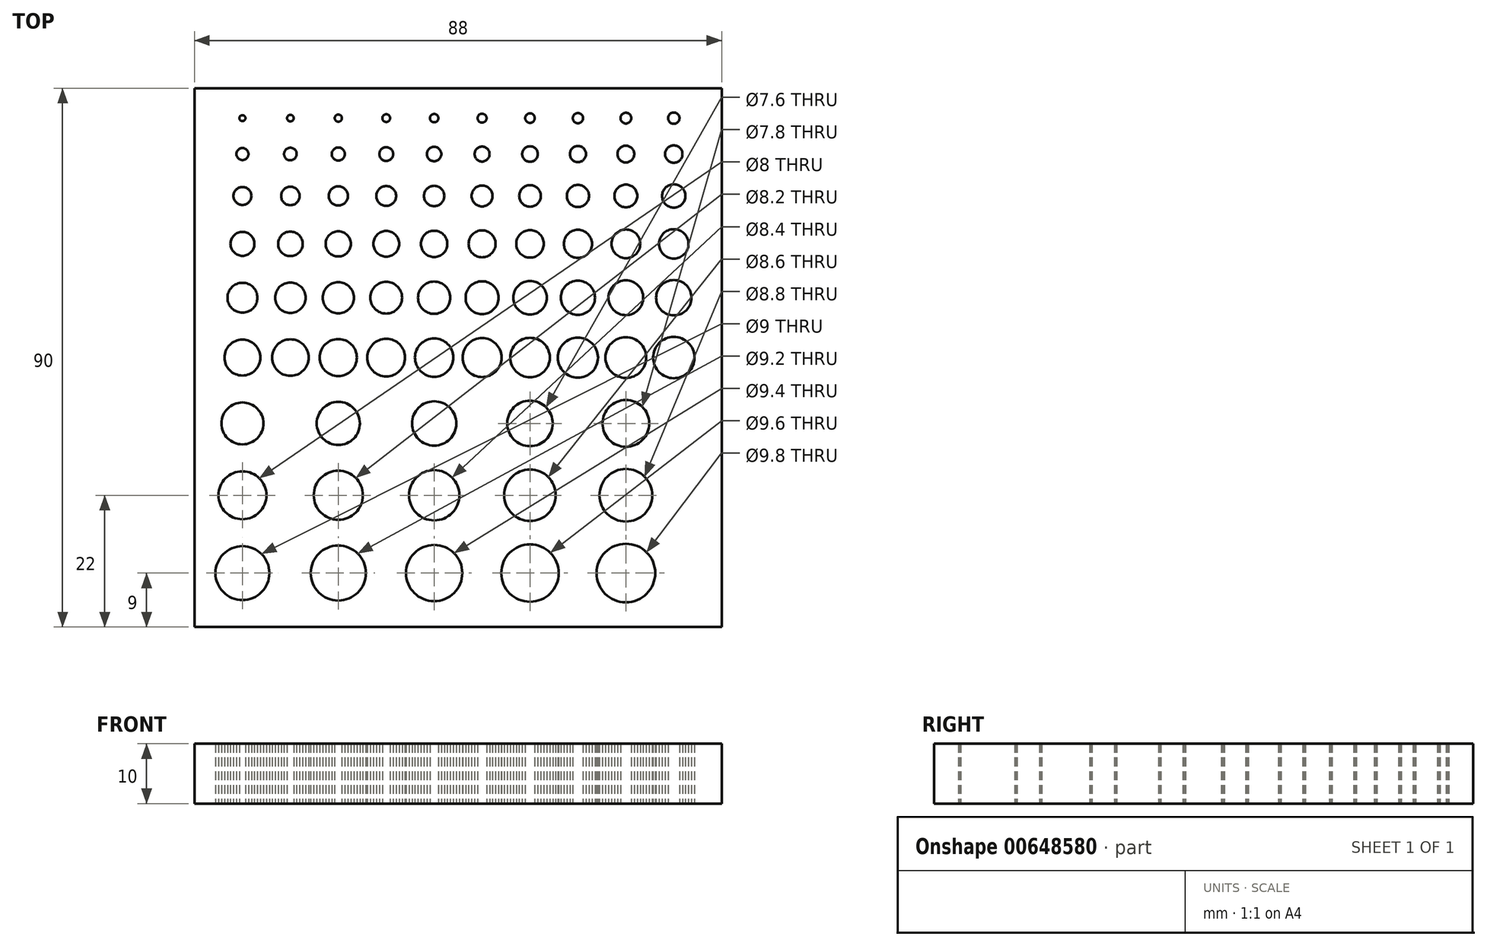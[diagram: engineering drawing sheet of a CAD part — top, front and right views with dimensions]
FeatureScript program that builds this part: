
annotation { "Feature Type Name" : "Feature", "Feature Type Description" : "" }
export const myFeature = defineFeature(function(context is Context, id is Id, definition is map)
    precondition{}
    {
        {
            var Q0;
            Q0=qCreatedBy(makeId("Top.planeOp"),FACE);
            var sketch = newSketch(context, id + "F0", { "sketchPlane" : qUnion([Q0])});
            skLineSegment(sketch, "E0.bottom", {"start": v(44, -45) * mm, "end": v(-44, -45) * mm});
            skLineSegment(sketch, "E0.top", {"start": v(44, 45) * mm, "end": v(-44, 45) * mm});
            skLineSegment(sketch, "E0.left", {"start": v(44, -45) * mm, "end": v(44, 45) * mm});
            skLineSegment(sketch, "E0.right", {"start": v(-44, -45) * mm, "end": v(-44, 45) * mm});
            skPoint(sketch, "E0.middle", {"position": v(0, 0) * mm});
            skLineSegment(sketch, "E1", {"start": v(-44, 40) * mm, "end": v(44, 40) * mm, "construction": true});
            skLineSegment(sketch, "E2", {"start": v(-44, 34) * mm, "end": v(44, 34) * mm, "construction": true});
            skLineSegment(sketch, "E3", {"start": v(-44, 27) * mm, "end": v(44, 27) * mm, "construction": true});
            skLineSegment(sketch, "E4", {"start": v(-44, 19) * mm, "end": v(44, 19) * mm, "construction": true});
            skLineSegment(sketch, "E5", {"start": v(-44, 10) * mm, "end": v(44, 10) * mm, "construction": true});
            skLineSegment(sketch, "E6", {"start": v(-44, 0) * mm, "end": v(44, 0) * mm, "construction": true});
            skLineSegment(sketch, "E7", {"start": v(-44, -11) * mm, "end": v(44, -11) * mm, "construction": true});
            skLineSegment(sketch, "E8", {"start": v(-44, -23) * mm, "end": v(44, -23) * mm, "construction": true});
            skLineSegment(sketch, "E9", {"start": v(-44, -36) * mm, "end": v(44, -36) * mm, "construction": true});
            skLineSegment(sketch, "E10", {"start": v(-44, -46) * mm, "end": v(44, -46) * mm, "construction": true});
            skLineSegment(sketch, "E11", {"start": v(-36, 45) * mm, "end": v(-36, -45) * mm, "construction": true});
            skLineSegment(sketch, "E12", {"start": v(-28, 45) * mm, "end": v(-28, -45) * mm, "construction": true});
            skLineSegment(sketch, "E13", {"start": v(-20, 45) * mm, "end": v(-20, -45) * mm, "construction": true});
            skLineSegment(sketch, "E14", {"start": v(-12, 45) * mm, "end": v(-12, -45) * mm, "construction": true});
            skLineSegment(sketch, "E15", {"start": v(36, 45) * mm, "end": v(36, -45) * mm, "construction": true});
            skLineSegment(sketch, "E16", {"start": v(-4, -45) * mm, "end": v(-4, 45) * mm, "construction": true});
            skLineSegment(sketch, "E17", {"start": v(4, 45) * mm, "end": v(4, -45) * mm, "construction": true});
            skLineSegment(sketch, "E18", {"start": v(12, 45) * mm, "end": v(12, -45) * mm, "construction": true});
            skLineSegment(sketch, "E19", {"start": v(20, 45) * mm, "end": v(20, -45) * mm, "construction": true});
            skLineSegment(sketch, "E20", {"start": v(28, 45) * mm, "end": v(28, -45) * mm, "construction": true});
            skCircle(sketch, "E21", {"center": v(-36, 40) * mm, "radius": 0.5 * mm});
            skCircle(sketch, "E22", {"center": v(-28, 40) * mm, "radius": 0.55 * mm});
            skCircle(sketch, "E23", {"center": v(-20, 40) * mm, "radius": 0.6 * mm});
            skCircle(sketch, "E24", {"center": v(-12, 40) * mm, "radius": 0.65 * mm});
            skCircle(sketch, "E25", {"center": v(-4, 40) * mm, "radius": 0.7 * mm});
            skCircle(sketch, "E26", {"center": v(4, 40) * mm, "radius": 0.75 * mm});
            skCircle(sketch, "E27", {"center": v(12, 40) * mm, "radius": 0.8 * mm});
            skCircle(sketch, "E28", {"center": v(20, 40) * mm, "radius": 0.85 * mm});
            skCircle(sketch, "E29", {"center": v(28, 40) * mm, "radius": 0.9 * mm});
            skCircle(sketch, "E30", {"center": v(36, 40) * mm, "radius": 0.95 * mm});
            skCircle(sketch, "E31", {"center": v(-36, 34) * mm, "radius": 1 * mm});
            skCircle(sketch, "E32", {"center": v(-28, 34) * mm, "radius": 1.05 * mm});
            skCircle(sketch, "E33", {"center": v(-20, 34) * mm, "radius": 1.1 * mm});
            skCircle(sketch, "E34", {"center": v(-12, 34) * mm, "radius": 1.15 * mm});
            skCircle(sketch, "E35", {"center": v(-4, 34) * mm, "radius": 1.2 * mm});
            skCircle(sketch, "E36", {"center": v(4, 34) * mm, "radius": 1.25 * mm});
            skCircle(sketch, "E37", {"center": v(12, 34) * mm, "radius": 1.3 * mm});
            skCircle(sketch, "E38", {"center": v(20, 34) * mm, "radius": 1.35 * mm});
            skCircle(sketch, "E39", {"center": v(28, 34) * mm, "radius": 1.4 * mm});
            skCircle(sketch, "E40", {"center": v(36, 34) * mm, "radius": 1.45 * mm});
            skCircle(sketch, "E41", {"center": v(-36, 27) * mm, "radius": 1.5 * mm});
            skCircle(sketch, "E42", {"center": v(-28, 27) * mm, "radius": 1.55 * mm});
            skCircle(sketch, "E43", {"center": v(-20, 27) * mm, "radius": 1.6 * mm});
            skCircle(sketch, "E44", {"center": v(-12, 27) * mm, "radius": 1.65 * mm});
            skCircle(sketch, "E45", {"center": v(-4, 27) * mm, "radius": 1.7 * mm});
            skCircle(sketch, "E46", {"center": v(4, 27) * mm, "radius": 1.75 * mm});
            skCircle(sketch, "E47", {"center": v(12, 27) * mm, "radius": 1.8 * mm});
            skCircle(sketch, "E48", {"center": v(20, 27) * mm, "radius": 1.85 * mm});
            skCircle(sketch, "E49", {"center": v(28, 27) * mm, "radius": 1.9 * mm});
            skCircle(sketch, "E50", {"center": v(36, 27) * mm, "radius": 1.95 * mm});
            skCircle(sketch, "E51", {"center": v(-36, 19) * mm, "radius": 2 * mm});
            skCircle(sketch, "E52", {"center": v(-28, 19) * mm, "radius": 2.05 * mm});
            skCircle(sketch, "E53", {"center": v(-20, 19) * mm, "radius": 2.1 * mm});
            skCircle(sketch, "E54", {"center": v(-12, 19) * mm, "radius": 2.15 * mm});
            skCircle(sketch, "E55", {"center": v(-4, 19) * mm, "radius": 2.2 * mm});
            skCircle(sketch, "E56", {"center": v(4, 19) * mm, "radius": 2.25 * mm});
            skCircle(sketch, "E57", {"center": v(12, 19) * mm, "radius": 2.3 * mm});
            skCircle(sketch, "E58", {"center": v(20, 19) * mm, "radius": 2.35 * mm});
            skCircle(sketch, "E59", {"center": v(28, 19) * mm, "radius": 2.4 * mm});
            skCircle(sketch, "E60", {"center": v(36, 19) * mm, "radius": 2.45 * mm});
            skCircle(sketch, "E61", {"center": v(-36, 10) * mm, "radius": 2.5 * mm});
            skCircle(sketch, "E62", {"center": v(-28, 10) * mm, "radius": 2.55 * mm});
            skCircle(sketch, "E63", {"center": v(-20, 10) * mm, "radius": 2.6 * mm});
            skCircle(sketch, "E64", {"center": v(-12, 10) * mm, "radius": 2.65 * mm});
            skCircle(sketch, "E65", {"center": v(-4, 10) * mm, "radius": 2.7 * mm});
            skCircle(sketch, "E66", {"center": v(4, 10) * mm, "radius": 2.75 * mm});
            skCircle(sketch, "E67", {"center": v(12, 10) * mm, "radius": 2.8 * mm});
            skCircle(sketch, "E68", {"center": v(20, 10) * mm, "radius": 2.85 * mm});
            skCircle(sketch, "E69", {"center": v(28, 10) * mm, "radius": 2.9 * mm});
            skCircle(sketch, "E70", {"center": v(36, 10) * mm, "radius": 2.95 * mm});
            skCircle(sketch, "E71", {"center": v(-36, 0) * mm, "radius": 3 * mm});
            skCircle(sketch, "E72", {"center": v(-28, 0) * mm, "radius": 3.05 * mm});
            skCircle(sketch, "E73", {"center": v(-20, 0) * mm, "radius": 3.1 * mm});
            skCircle(sketch, "E74", {"center": v(-12, 0) * mm, "radius": 3.15 * mm});
            skCircle(sketch, "E75", {"center": v(-4, 0) * mm, "radius": 3.2 * mm});
            skCircle(sketch, "E76", {"center": v(4, 0) * mm, "radius": 3.25 * mm});
            skCircle(sketch, "E77", {"center": v(12, 0) * mm, "radius": 3.3 * mm});
            skCircle(sketch, "E78", {"center": v(20, 0) * mm, "radius": 3.35 * mm});
            skCircle(sketch, "E79", {"center": v(28, 0) * mm, "radius": 3.4 * mm});
            skCircle(sketch, "E80", {"center": v(36, 0) * mm, "radius": 3.45 * mm});
            skCircle(sketch, "E81", {"center": v(-36, -11) * mm, "radius": 3.5 * mm});
            skCircle(sketch, "E82", {"center": v(-20, -11) * mm, "radius": 3.6 * mm});
            skCircle(sketch, "E83", {"center": v(-4, -11) * mm, "radius": 3.7 * mm});
            skCircle(sketch, "E84", {"center": v(12, -11) * mm, "radius": 3.8 * mm});
            skCircle(sketch, "E85", {"center": v(28, -11) * mm, "radius": 3.9 * mm});
            skCircle(sketch, "E86", {"center": v(-36, -23) * mm, "radius": 4 * mm});
            skCircle(sketch, "E87", {"center": v(-20, -23) * mm, "radius": 4.1 * mm});
            skCircle(sketch, "E88", {"center": v(-4, -23) * mm, "radius": 4.2 * mm});
            skCircle(sketch, "E89", {"center": v(12, -23) * mm, "radius": 4.3 * mm});
            skCircle(sketch, "E90", {"center": v(28, -23) * mm, "radius": 4.4 * mm});
            skCircle(sketch, "E91", {"center": v(-36, -36) * mm, "radius": 4.5 * mm});
            skCircle(sketch, "E92", {"center": v(-20, -36) * mm, "radius": 4.6 * mm});
            skCircle(sketch, "E93", {"center": v(-4, -36) * mm, "radius": 4.7 * mm});
            skCircle(sketch, "E94", {"center": v(12, -36) * mm, "radius": 4.8 * mm});
            skCircle(sketch, "E95", {"center": v(28, -36) * mm, "radius": 4.9 * mm});
            skSolve(sketch);
        }
        {
            var Q0;
            Q0=makeQuery(id+"F0.imprint","IMPRINT",FACE,{"disambiguationData":[TD([[makeQuery(id+"F0.imprint","IMPRINT",EDGE,{"derivedFrom":sQuery(id+"F0.wireOp",EDGE,"E0.bottom")}),-1.0]])]});
            extrude(context, id + "F1", {"entities" : qUnion([Q0]), "depth" : 10 * mm, "offsetDistance" : 25 * mm});
        }
    });
